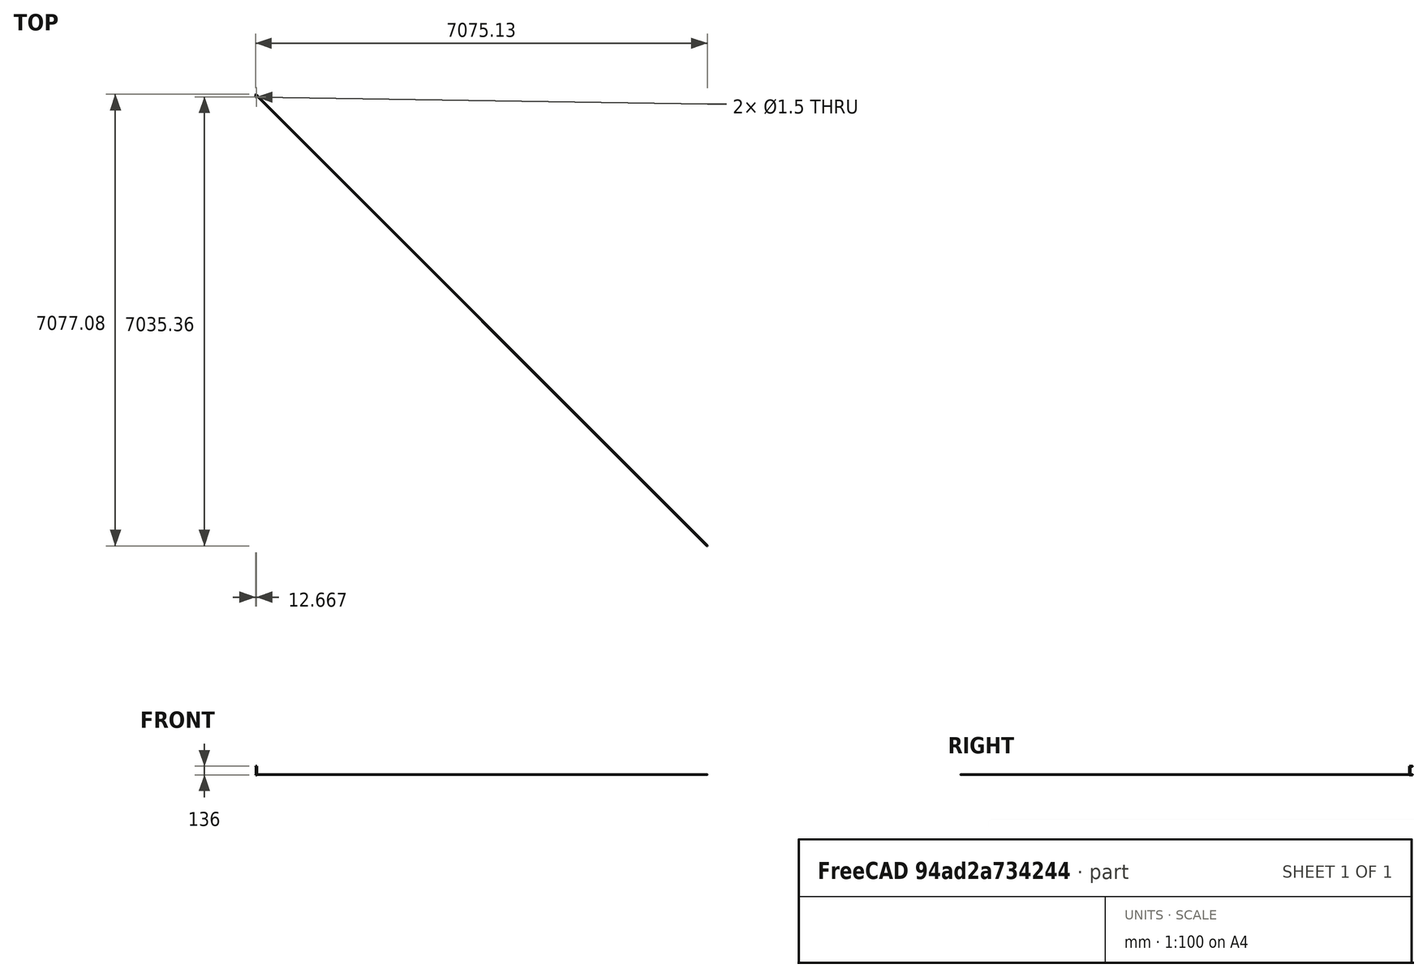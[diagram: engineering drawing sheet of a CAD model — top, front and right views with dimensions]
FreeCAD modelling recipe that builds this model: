
FCSTD DOCUMENT  (FreeCAD 0.16R6712 (Git))
Label: Guignol_Moteurs_Arriere
License: All rights reserved
LicenseURL: http://en.wikipedia.org/wiki/All_rights_reserved
objects: Sketcher::SketchObject×10, PartDesign::Pocket×6, PartDesign::Pad×4, Part::MultiFuse×3, Mesh::Feature×2
note: 33 computed .brp shape members not serialized (recipe doc carries the construction recipe); baked Part::Feature solids carry a one-line shape summary decoded from their .brp

FEATURE [Sketcher::SketchObject] Sketch
  sketch-geometry (9):
    g0: LineSegment StartX=0 StartY=0 StartZ=0 EndX=7.07107 EndY=7.07107 EndZ=0
    g1: LineSegment StartX=0 StartY=0 StartZ=0 EndX=4.59619 EndY=-4.59619 EndZ=0
    g2: LineSegment StartX=4.59619 StartY=-4.59619 StartZ=0 EndX=11.6673 EndY=2.47487 EndZ=0
    g3: LineSegment StartX=11.6673 StartY=2.47487 StartZ=0 EndX=11.6673 EndY=-42.5251 EndZ=0
    g4: LineSegment StartX=-3 StartY=1.24264 StartZ=0 EndX=-3 EndY=-4.59619 EndZ=0
    g5: LineSegment StartX=-3 StartY=-4.59619 StartZ=0 EndX=11.6673 EndY=-42.5251 EndZ=0
    g6: LineSegment [constr] StartX=4.59619 StartY=-4.59619 StartZ=0 EndX=-3 EndY=-4.59619 EndZ=0
    g7: LineSegment StartX=-3 StartY=1.24264 StartZ=0 EndX=4.94975 EndY=9.19239 EndZ=0
    g8: LineSegment StartX=4.94975 StartY=9.19239 StartZ=0 EndX=7.07107 EndY=7.07107 EndZ=0
  constraints (26):
    c: Coincident(g0,g-1)
    c: Coincident(g1,g-1)
    c: Coincident(g1,g2)
    c: Coincident(g3,g2)
    c: Vertical(g3)
    c: Vertical(g4)
    c: Coincident(g5,g4)
    c: Coincident(g5,g3)
    c: DistanceX(g4,g-1) = 3
    c: Coincident(g6,g1)
    c: Angle(g-2,g6) = 1.5708
    c: Coincident(g4,g6)
    c: DistanceY(g3,g3) = 45
    c: Angle(g2,g3) = 0.785398
    c: Parallel(g0,g2)
    c: Distance(g2) = 10
    c: Distance(g0) = 10
    c: Distance(g1) = 6.5
    c: Angle(g2,g1) = 1.5708
    c: PointOnObject(g7,g4)
    c: Coincident(g8,g7)
    c: Coincident(g8,g0)
    c: Angle(g8,g0) = 1.5708
    c: Distance(g8) = 3
    c: Coincident(g4,g7)
    c: Parallel(g0,g7)
FEATURE [PartDesign::Pad] Pad
  Length = 5
  Length2 = 100
  Sketch = -> Sketch
  Type = 0
FEATURE [Sketcher::SketchObject] Sketch001
  ExternalGeometry = -> [Pad]
  Placement = pos=(-2.12132,2.12132,0) rot=(-0.281085,0.678598,0.678598;3.68962rad)
  Support = -> Pad [Face8]
  sketch-geometry (1):
    g0: Circle CenterX=-3 CenterY=2.5 CenterZ=0 NormalX=0 NormalY=0 NormalZ=1 Radius=1.5
  constraints (3):
    c: Radius(g0) = 1.5
    c: DistanceY(g-1,g0) = 2.5
    c: DistanceX(g-3,g0) = 7
FEATURE [PartDesign::Pocket] Pocket
  Length = 5
  Sketch = -> Sketch001
  Type = 1
FEATURE [Sketcher::SketchObject] Sketch002
  ExternalGeometry = -> [Pocket]
  Placement = pos=(0,0,5) rot=(0,0,1;0rad)
  Support = -> Pocket [Face5]
  sketch-geometry (5):
    g0: LineSegment StartX=4.28467 StartY=-9.57117 StartZ=0 EndX=16.3307 EndY=2.47487 EndZ=0
    g1: LineSegment StartX=4.28467 StartY=-9.57117 StartZ=0 EndX=16.3307 EndY=-40.7217 EndZ=0
    g2: LineSegment StartX=16.3307 StartY=-40.7217 StartZ=0 EndX=16.3307 EndY=2.47487 EndZ=0
    g3: LineSegment [constr] StartX=16.3307 StartY=-40.7217 StartZ=0 EndX=11.6673 EndY=-42.5251 EndZ=0
    g4: LineSegment [constr] StartX=11.6673 StartY=2.47487 StartZ=0 EndX=16.3307 EndY=2.47487 EndZ=0
  constraints (13):
    c: Coincident(g1,g0)
    c: Coincident(g2,g0)
    c: Vertical(g2)
    c: Parallel(g0,g-3)
    c: Parallel(g1,g-4)
    c: Coincident(g1,g2)
    c: Coincident(g3,g1)
    c: Coincident(g3,g-4)
    c: Angle(g3,g-4) = 1.5708
    c: Distance(g3) = 5
    c: Coincident(g4,g-3)
    c: Horizontal(g4)
    c: Coincident(g0,g4)
FEATURE [PartDesign::Pocket] Pocket001
  Length = 5
  Sketch = -> Sketch002
  Type = 0
FEATURE [Sketcher::SketchObject] Sketch003
  Placement = pos=(0,0,131) rot=(0,0,1;0rad)
  sketch-geometry (9):
    g0: LineSegment StartX=0 StartY=0 StartZ=0 EndX=7.07107 EndY=7.07107 EndZ=0
    g1: LineSegment StartX=0 StartY=0 StartZ=0 EndX=4.59619 EndY=-4.59619 EndZ=0
    g2: LineSegment StartX=4.59619 StartY=-4.59619 StartZ=0 EndX=11.6673 EndY=2.47487 EndZ=0
    g3: LineSegment StartX=11.6673 StartY=2.47487 StartZ=0 EndX=11.6673 EndY=-42.5251 EndZ=0
    g4: LineSegment StartX=-3 StartY=1.24264 StartZ=0 EndX=-3 EndY=-4.59619 EndZ=0
    g5: LineSegment StartX=-3 StartY=-4.59619 StartZ=0 EndX=11.6673 EndY=-42.5251 EndZ=0
    g6: LineSegment [constr] StartX=4.59619 StartY=-4.59619 StartZ=0 EndX=-3 EndY=-4.59619 EndZ=0
    g7: LineSegment StartX=-3 StartY=1.24264 StartZ=0 EndX=4.94975 EndY=9.19239 EndZ=0
    g8: LineSegment StartX=4.94975 StartY=9.19239 StartZ=0 EndX=7.07107 EndY=7.07107 EndZ=0
  constraints (26):
    c: Coincident(g0,g-1)
    c: Coincident(g1,g-1)
    c: Coincident(g1,g2)
    c: Coincident(g3,g2)
    c: Vertical(g3)
    c: Vertical(g4)
    c: Coincident(g5,g4)
    c: Coincident(g5,g3)
    c: DistanceX(g4,g-1) = 3
    c: Coincident(g6,g1)
    c: Angle(g-2,g6) = 1.5708
    c: Coincident(g4,g6)
    c: DistanceY(g3,g3) = 45
    c: Angle(g2,g3) = 0.785398
    c: Parallel(g0,g2)
    c: Distance(g2) = 10
    c: Distance(g0) = 10
    c: Distance(g1) = 6.5
    c: Angle(g2,g1) = 1.5708
    c: PointOnObject(g7,g4)
    c: Coincident(g8,g7)
    c: Coincident(g8,g0)
    c: Angle(g8,g0) = 1.5708
    c: Distance(g8) = 3
    c: Coincident(g4,g7)
    c: Parallel(g0,g7)
FEATURE [PartDesign::Pad] Pad001
  Length = 5
  Length2 = 100
  Placement = pos=(0,0,131) rot=(0,0,1;0rad)
  Sketch = -> Sketch003
  Type = 0
FEATURE [Sketcher::SketchObject] Sketch004
  ExternalGeometry = -> [Pad001]
  Placement = pos=(-2.12132,2.12132,131) rot=(-0.281085,0.678598,0.678598;3.68962rad)
  Support = -> Pad001 [Face8]
  sketch-geometry (1):
    g0: Circle CenterX=-3 CenterY=2.5 CenterZ=0 NormalX=0 NormalY=0 NormalZ=1 Radius=1.5
  constraints (3):
    c: Radius(g0) = 1.5
    c: DistanceY(g-1,g0) = 2.5
    c: DistanceX(g-3,g0) = 7
FEATURE [PartDesign::Pocket] Pocket002
  Length = 5
  Placement = pos=(0,0,131) rot=(0,0,1;0rad)
  Sketch = -> Sketch004
  Type = 1
FEATURE [Sketcher::SketchObject] Sketch005
  ExternalGeometry = -> [Pocket002]
  Placement = pos=(0,0,136) rot=(0,0,1;0rad)
  Support = -> Pocket002 [Face5]
  sketch-geometry (5):
    g0: LineSegment StartX=4.28467 StartY=-9.57117 StartZ=0 EndX=16.3307 EndY=2.47487 EndZ=0
    g1: LineSegment StartX=4.28467 StartY=-9.57117 StartZ=0 EndX=16.3307 EndY=-40.7217 EndZ=0
    g2: LineSegment StartX=16.3307 StartY=-40.7217 StartZ=0 EndX=16.3307 EndY=2.47487 EndZ=0
    g3: LineSegment [constr] StartX=16.3307 StartY=-40.7217 StartZ=0 EndX=11.6673 EndY=-42.5251 EndZ=0
    g4: LineSegment [constr] StartX=11.6673 StartY=2.47487 StartZ=0 EndX=16.3307 EndY=2.47487 EndZ=0
  constraints (13):
    c: Coincident(g1,g0)
    c: Coincident(g2,g0)
    c: Vertical(g2)
    c: Parallel(g0,g-3)
    c: Parallel(g1,g-4)
    c: Coincident(g1,g2)
    c: Coincident(g3,g1)
    c: Coincident(g3,g-4)
    c: Angle(g3,g-4) = 1.5708
    c: Distance(g3) = 5
    c: Coincident(g4,g-3)
    c: Horizontal(g4)
    c: Coincident(g0,g4)
FEATURE [PartDesign::Pocket] Pocket003
  Length = 5
  Placement = pos=(0,0,131) rot=(0,0,1;0rad)
  Sketch = -> Sketch005
  Type = 0
FEATURE [Sketcher::SketchObject] Sketch006
  ExternalGeometry = -> [Pocket001]
  Placement = pos=(0,0,5) rot=(0,0,1;0rad)
  Support = -> Pocket001 [Face5]
  sketch-geometry (3):
    g0: LineSegment StartX=11.6673 StartY=-42.5251 StartZ=0 EndX=8.9622 EndY=-35.5299 EndZ=0
    g1: LineSegment StartX=8.9622 StartY=-35.5299 StartZ=0 EndX=11.6673 EndY=-34.4839 EndZ=0
    g2: LineSegment StartX=11.6673 StartY=-34.4839 StartZ=0 EndX=11.6673 EndY=-42.5251 EndZ=0
  constraints (8):
    c: Coincident(g1,g0)
    c: Coincident(g2,g0)
    c: Vertical(g2)
    c: Coincident(g1,g2)
    c: Coincident(g0,g-4)
    c: PointOnObject(g0,g-3)
    c: Angle(g1,g-3) = 1.5708
    c: Distance(g0,g0) = 7.5
FEATURE [PartDesign::Pad] Pad002
  Length = 131
  Length2 = 100
  Sketch = -> Sketch006
  Type = 0
FEATURE [Part::MultiFuse] Fusion
  Shapes = -> [Pad002,Pocket003]
FEATURE [Sketcher::SketchObject] Sketch007
  ExternalGeometry = -> [Fusion]
  Placement = pos=(0,0,136) rot=(0,0,1;0rad)
  Support = -> Fusion [Face34]
  sketch-geometry (1):
    g0: Circle CenterX=9.66726 CenterY=-32.5251 CenterZ=0 NormalX=0 NormalY=0 NormalZ=1 Radius=0.75
  constraints (3):
    c: DistanceY(g-3,g0) = 10
    c: Radius(g0) = 0.75
    c: DistanceX(g0,g-3) = 2
FEATURE [PartDesign::Pocket] Pocket004
  Length = 5
  Sketch = -> Sketch007
  Type = 1
FEATURE [Mesh::Feature] Bras_moteur  label="Bras_moteur_t"
  Placement = pos=(5,-0.5,200.5) rot=(0.678598,0.281085,0.678598;3.68963rad)
FEATURE [Part::MultiFuse] Fusion001
  Shapes = -> [Pocket004,Pad002]
FEATURE [Mesh::Feature] Bras_moteur001  label="Bras_moteur_b"
  Placement = pos=(5,-0.5,-64.5) rot=(-0.357407,0.862856,0.357407;1.71777rad)
FEATURE [Part::MultiFuse] Fusion002
  Shapes = -> [Pad002,Fusion001]
FEATURE [Sketcher::SketchObject] Sketch008
  ExternalGeometry = -> [Fusion002]
  Placement = pos=(0,0,0) rot=(1,0,0;3.14159rad)
  Support = -> Fusion002 [Face36]
  sketch-geometry (3):
    g0: LineSegment StartX=11.6673 StartY=42.5251 StartZ=0 EndX=11.6673 EndY=28.6622 EndZ=0
    g1: LineSegment StartX=11.6673 StartY=28.6622 StartZ=0 EndX=16.3307 EndY=40.7217 EndZ=0
    g2: LineSegment StartX=16.3307 StartY=40.7217 StartZ=0 EndX=11.6673 EndY=42.5251 EndZ=0
  constraints (8):
    c: Coincident(g0,g-3)
    c: Vertical(g0)
    c: Coincident(g2,g1)
    c: Coincident(g0,g2)
    c: Coincident(g0,g-3)
    c: Angle(g2,g1) = 1.5708
    c: Coincident(g1,g0)
    c: Distance(g2) = 5
FEATURE [PartDesign::Pad] Pad003
  Length = 136
  Length2 = 100
  Reversed = true
  Sketch = -> Sketch008
  Type = 0
FEATURE [Sketcher::SketchObject] Sketch009
  ExternalGeometry = -> [Pad003]
  Placement = pos=(0.507563,0.196277,0) rot=(0.436162,0.636303,0.636303;2.31902rad)
  Support = -> Pad003 [Face23]
  sketch-geometry (4):
    g0: LineSegment StartX=-36.9411 StartY=131 StartZ=0 EndX=-30.9411 EndY=131 EndZ=0
    g1: LineSegment StartX=-30.9411 StartY=131 StartZ=0 EndX=-30.9411 EndY=5 EndZ=0
    g2: LineSegment StartX=-30.9411 StartY=5 StartZ=0 EndX=-36.9411 EndY=5 EndZ=0
    g3: LineSegment StartX=-36.9411 StartY=5 StartZ=0 EndX=-36.9411 EndY=131 EndZ=0
  constraints (11):
    c: Coincident(g0,g1)
    c: Coincident(g1,g2)
    c: Coincident(g2,g3)
    c: Coincident(g3,g0)
    c: Horizontal(g0)
    c: Horizontal(g2)
    c: Vertical(g1)
    c: Vertical(g3)
    c: Coincident(g0,g-3)
    c: Coincident(g1,g-3)
    c: DistanceX(g2,g2) = 6
FEATURE [PartDesign::Pocket] Pocket005
  Length = 5
  Sketch = -> Sketch009
  Type = 0
